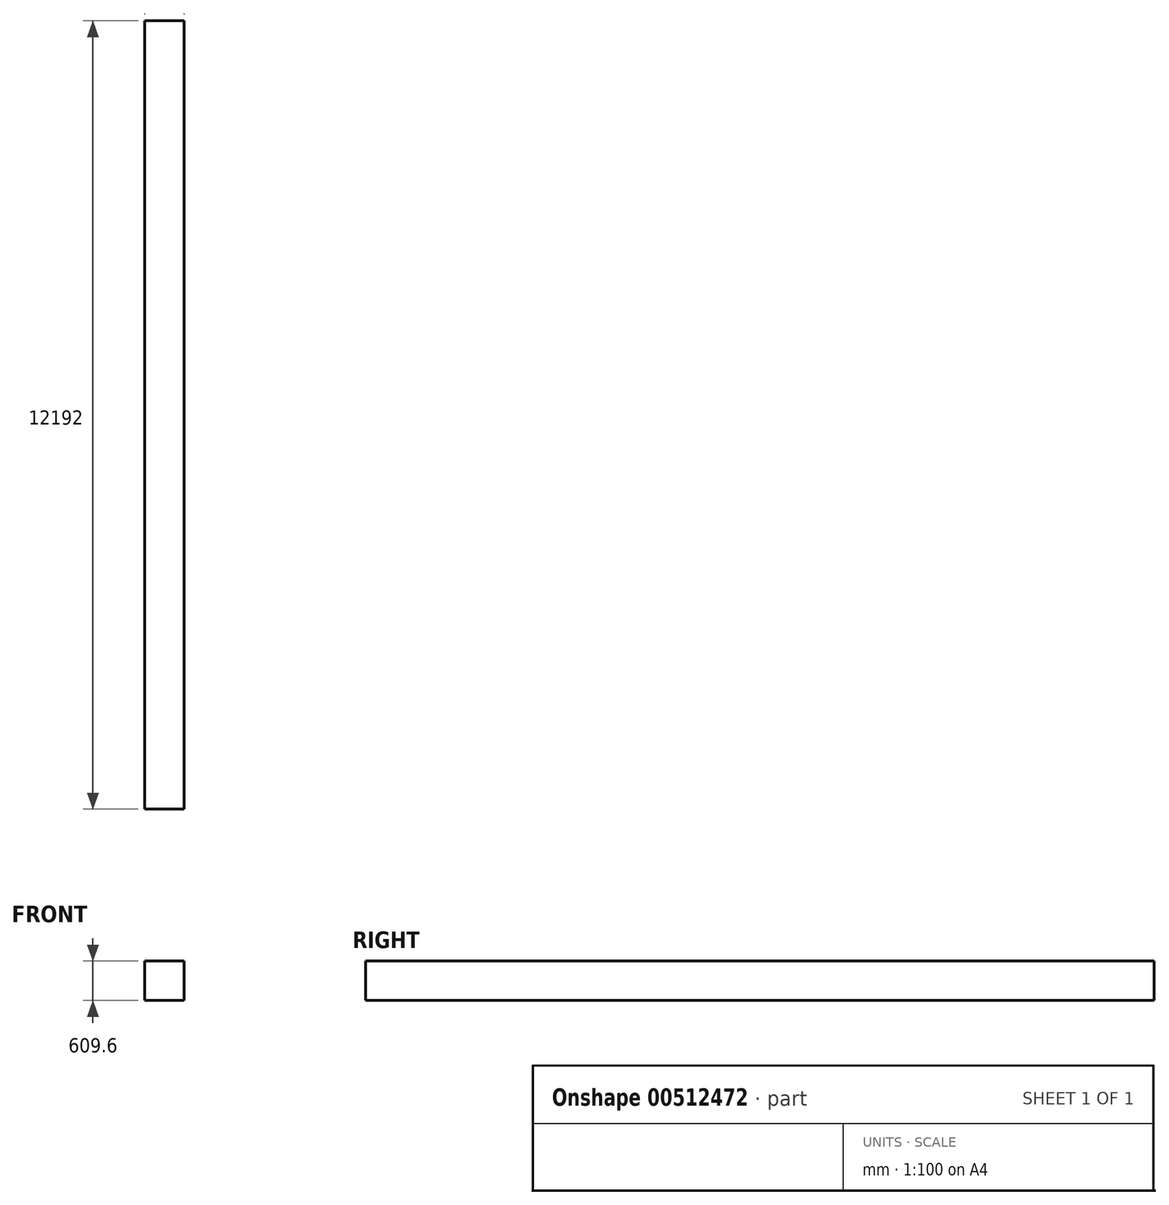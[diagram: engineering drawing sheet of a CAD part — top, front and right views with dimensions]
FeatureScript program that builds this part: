
annotation { "Feature Type Name" : "Feature", "Feature Type Description" : "" }
export const myFeature = defineFeature(function(context is Context, id is Id, definition is map)
    precondition{}
    {
        {
            var Q0;
            Q0=qCreatedBy(makeId("Top.planeOp"),FACE);
            var sketch = newSketch(context, id + "F0", { "sketchPlane" : qUnion([Q0])});
            skLineSegment(sketch, "E0.bottom", {"start": v(0, 12192) * mm, "end": v(609.6, 12192) * mm});
            skLineSegment(sketch, "E0.top", {"start": v(0, 0) * mm, "end": v(609.6, 0) * mm});
            skLineSegment(sketch, "E0.left", {"start": v(0, 12192) * mm, "end": v(0, 0) * mm});
            skLineSegment(sketch, "E0.right", {"start": v(609.6, 12192) * mm, "end": v(609.6, 0) * mm});
            skSolve(sketch);
        }
        {
            var Q0;
            Q0 = qSketchRegion(id + "F0", true);
            extrude(context, id + "F1", {"entities" : qUnion([Q0]), "depth" : 609.6 * mm});
        }
    });
